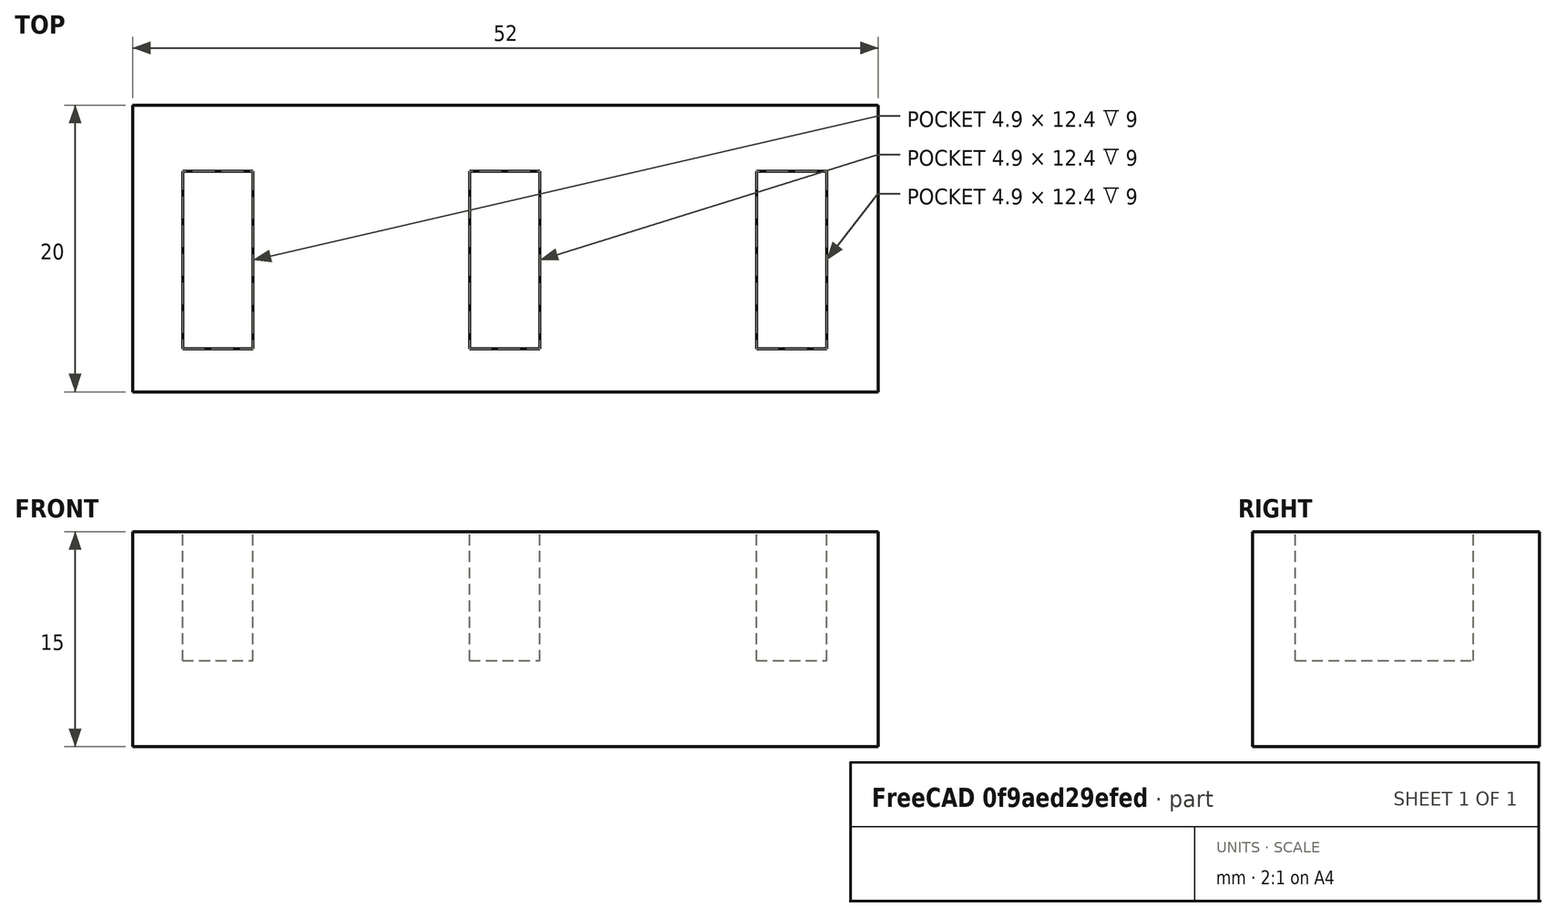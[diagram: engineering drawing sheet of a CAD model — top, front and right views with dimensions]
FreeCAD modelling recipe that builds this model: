
FCSTD DOCUMENT  (FreeCAD 1.0R38806 (Git))
Label: reto_4
License: All rights reserved
LicenseURL: https://en.wikipedia.org/wiki/All_rights_reserved
objects: Part::Box×4, Part::Cut×3
note: 7 computed .brp shape members not serialized (recipe doc carries the construction recipe); baked Part::Feature solids carry a one-line shape summary decoded from their .brp

FEATURE [Part::Box] Box  label="Cube"
  AttacherType = Attacher::AttachEngine3D
  Height = 15
  Length = 52
  Width = 20
FEATURE [Part::Box] Box001  label="Cube001"
  AttacherType = Attacher::AttachEngine3D
  Height = 10
  Length = 4.9
  Placement = pos=(3.5,3,6) rot=(0,0,1;0rad)
  Width = 12.4
FEATURE [Part::Box] Box002  label="Cube002"
  AttacherType = Attacher::AttachEngine3D
  Height = 10
  Length = 4.9
  Placement = pos=(23.5,3,6) rot=(0,0,1;0rad)
  Width = 12.4
FEATURE [Part::Box] Box003  label="Cube003"
  AttacherType = Attacher::AttachEngine3D
  Height = 10
  Length = 4.9
  Placement = pos=(43.5,3,6) rot=(0,0,1;0rad)
  Width = 12.4
FEATURE [Part::Cut] Cut
  Base = -> Box
  Refine = true
  Tool = -> Box001
FEATURE [Part::Cut] Cut001
  Base = -> Cut
  Refine = true
  Tool = -> Box002
FEATURE [Part::Cut] Cut002
  Base = -> Cut001
  Refine = true
  Tool = -> Box003
